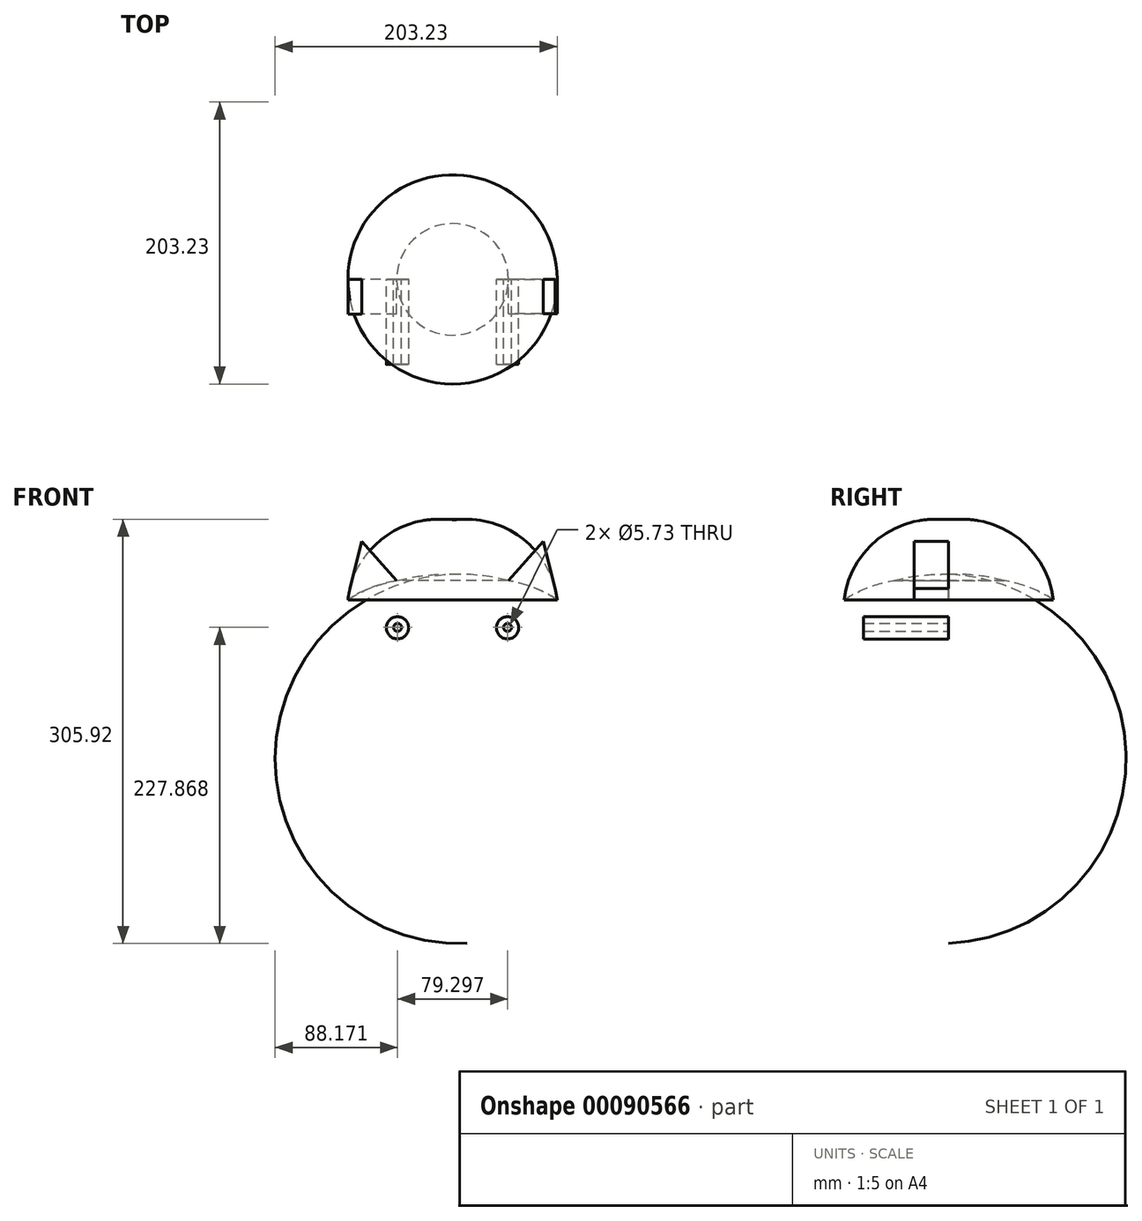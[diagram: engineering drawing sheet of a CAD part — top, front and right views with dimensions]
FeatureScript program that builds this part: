
annotation { "Feature Type Name" : "Feature", "Feature Type Description" : "" }
export const myFeature = defineFeature(function(context is Context, id is Id, definition is map)
    precondition{}
    {
        {
            var Q0;
            Q0=qCreatedBy(makeId("Front.planeOp"),FACE);
            var sketch = newSketch(context, id + "F0", { "sketchPlane" : qUnion([Q0])});
            skArc(sketch, "E0", {"start": v(0, 26.67) * mm, "mid": v(-20.28, 25.93) * mm, "end": v(-40.22, 22.1) * mm});
            skLineSegment(sketch, "E1", {"start": v(-40.22, 22.1) * mm, "end": v(-65.32, 50.63) * mm});
            skLineSegment(sketch, "E2", {"start": v(-65.32, 50.63) * mm, "end": v(-73.88, 16.69) * mm});
            skArc(sketch, "E3", {"start": v(-73.88, 16.69) * mm, "mid": v(-58.74, -43.77) * mm, "end": v(0, -64.6) * mm});
            skLineSegment(sketch, "E4", {"start": v(0, 26.67) * mm, "end": v(0, -64.6) * mm});
            skArc(sketch, "E5", {"start": v(-40.22, 22.1) * mm, "mid": v(-58.55, 17.12) * mm, "end": v(-75.41, 8.37) * mm});
            skLineSegment(sketch, "E6.MirrorCS", {"start": v(40.22, 22.1) * mm, "end": v(65.32, 50.63) * mm});
            skLineSegment(sketch, "E7.MirrorCS", {"start": v(65.32, 50.63) * mm, "end": v(73.88, 16.69) * mm});
            skArc(sketch, "E8.MirrorCS", {"start": v(40.22, 22.1) * mm, "mid": v(58.55, 17.12) * mm, "end": v(75.41, 8.37) * mm});
            skLineSegment(sketch, "E9", {"start": v(73.88, 16.69) * mm, "end": v(75.41, 8.37) * mm});
            skSolve(sketch);
        }
        {
            var Q0;
            Q0=makeQuery(id+"F0.imprint","IMPRINT",FACE,{"disambiguationData":[TD([[makeQuery(id+"F0.imprint","IMPRINT",EDGE,{"derivedFrom":sQuery(id+"F0.wireOp",EDGE,"E0")}),1.0]])]});
            var Q1;
            Q1=sQuery(id+"F0.wireOp",EDGE,"E4");
            revolve(context, id + "F1", {"entities" : qUnion([Q0]), "axis" : qUnion([Q1]), "revolveType" : RevolveType.FULL});
        }
        {
            var Q0;
            Q0=makeQuery(id+"F0.imprint","IMPRINT",FACE,{"disambiguationData":[TD([[makeQuery(id+"F0.imprint","IMPRINT",EDGE,{"derivedFrom":sQuery(id+"F0.wireOp",EDGE,"E6.MirrorCS")}),-1.0]])]});
            extrude(context, id + "F2", {"entities" : qUnion([Q0]), "depth" : 24.86 * mm});
        }
        {
            var Q0;
            Q0=makeQuery(id+"F0.imprint","IMPRINT",FACE,{"disambiguationData":[TD([[makeQuery(id+"F0.imprint","IMPRINT",EDGE,{"derivedFrom":sQuery(id+"F0.wireOp",EDGE,"E1")}),1.0]])]});
            extrude(context, id + "F3", {"entities" : qUnion([Q0]), "depth" : 25.05 * mm});
        }
        {
            var Q0;
            Q0=qCreatedBy(makeId("Front.planeOp"),FACE);
            var sketch = newSketch(context, id + "F4", { "sketchPlane" : qUnion([Q0])});
            skCircle(sketch, "E10", {"center": v(-39.36, -12.7) * mm, "radius": 13.15 * mm});
            skCircle(sketch, "E11.MirrorC", {"center": v(39.36, -12.7) * mm, "radius": 13.15 * mm});
            skSolve(sketch);
        }
        {
            var Q0;
            Q0 = qSketchRegion(id + "F4", true);
            extrude(context, id + "F5", {"entities" : qUnion([Q0]), "operationType" : NewBodyOperationType.REMOVE, "endBound" : BoundingType.THROUGH_ALL, "depth" : 25.4 * mm, "hasSecondDirection" : true, "secondDirectionOppositeDirection" : true, "secondDirectionDepth" : 25.4 * mm});
        }
        {
            var Q0;
            Q0=qCreatedBy(makeId("Right.planeOp"),FACE);
            var sketch = newSketch(context, id + "F6", { "sketchPlane" : qUnion([Q0])});
            skArc(sketch, "E12", {"start": v(-81.86, -29.8) * mm, "mid": v(-76.97, -18.58) * mm, "end": v(-75.59, -6.42) * mm});
            skArc(sketch, "E13", {"start": v(-81.86, -29.8) * mm, "mid": v(-70.43, -42.74) * mm, "end": v(-54.2, -48.63) * mm});
            skLineSegment(sketch, "E14", {"start": v(-75.59, -6.42) * mm, "end": v(-54.2, -48.63) * mm});
            skSolve(sketch);
        }
        {
            var Q0;
            Q0=makeQuery(id+"F6.imprint","IMPRINT",FACE,{"disambiguationData":[TD([[makeQuery(id+"F6.imprint","IMPRINT",EDGE,{"derivedFrom":sQuery(id+"F6.wireOp",EDGE,"E12")}),-1.0]])]});
            var Q1;
            Q1=sQuery(id+"F6.wireOp",EDGE,"E14");
            revolve(context, id + "F7", {"operationType" : NewBodyOperationType.ADD, "entities" : qUnion([Q0]), "axis" : qUnion([Q1]), "revolveType" : RevolveType.FULL});
        }
        {
            var Q0;
            Q0=qCreatedBy(makeId("Front.planeOp"),FACE);
            var sketch = newSketch(context, id + "F8", { "sketchPlane" : qUnion([Q0])});
            skCircle(sketch, "E15", {"center": v(-39.65, -11.84) * mm, "radius": 8.03 * mm});
            skCircle(sketch, "E16.MirrorC", {"center": v(39.65, -11.84) * mm, "radius": 8.03 * mm});
            skSolve(sketch);
        }
        {
            var Q0;
            Q0 = qSketchRegion(id + "F8", true);
            extrude(context, id + "F9", {"entities" : qUnion([Q0]), "depth" : 61.37 * mm});
        }
        {
            var Q0;
            Q0=qCreatedBy(makeId("Front.planeOp"),FACE);
            var sketch = newSketch(context, id + "F10", { "sketchPlane" : qUnion([Q0])});
            skCircle(sketch, "E17", {"center": v(-39.65, -11.55) * mm, "radius": 2.87 * mm});
            skCircle(sketch, "E18.MirrorC", {"center": v(39.65, -11.55) * mm, "radius": 2.87 * mm});
            skSolve(sketch);
        }
        {
            var Q0;
            Q0 = qSketchRegion(id + "F10", true);
            extrude(context, id + "F11", {"entities" : qUnion([Q0]), "operationType" : NewBodyOperationType.REMOVE, "depth" : 76.2 * mm});
        }
        {
            var Q0;
            Q0=sQuery(id+"F10.wireOp",EDGE,"E17");
            var Q1;
            Q1=sQuery(id+"F10.wireOp",EDGE,"E18.MirrorC");
            extrude(context, id + "F12", {"bodyType" : ToolBodyType.SURFACE, "surfaceEntities" : qUnion([Q0, Q1]), "depth" : 62.08 * mm});
        }
        {
            var Q0;
            Q0=qCreatedBy(makeId("Front.planeOp"),FACE);
            var sketch = newSketch(context, id + "F13", { "sketchPlane" : qUnion([Q0])});
            skArc(sketch, "E19", {"start": v(-13.7, -34.37) * mm, "mid": v(-6.44, -38.64) * mm, "end": v(0, -33.23) * mm});
            skArc(sketch, "E20", {"start": v(-13.7, -34.37) * mm, "mid": v(-8.44, -42.8) * mm, "end": v(0, -48.06) * mm});
            skArc(sketch, "E21.MirrorCS", {"start": v(13.7, -34.37) * mm, "mid": v(6.44, -38.64) * mm, "end": v(0, -33.23) * mm});
            skArc(sketch, "E22.MirrorCS", {"start": v(13.7, -34.37) * mm, "mid": v(8.44, -42.8) * mm, "end": v(0, -48.06) * mm});
            skSolve(sketch);
        }
        {
            var Q0;
            Q0 = qSketchRegion(id + "F13", true);
            extrude(context, id + "F14", {"entities" : qUnion([Q0]), "operationType" : NewBodyOperationType.REMOVE, "depth" : 25.4 * mm});
        }
        {
            var Q0;
            Q0 = qSketchRegion(id + "F13", true);
            extrude(context, id + "F15", {"entities" : qUnion([Q0]), "operationType" : NewBodyOperationType.REMOVE, "endBound" : BoundingType.THROUGH_ALL, "depth" : 25.4 * mm});
        }
    });
